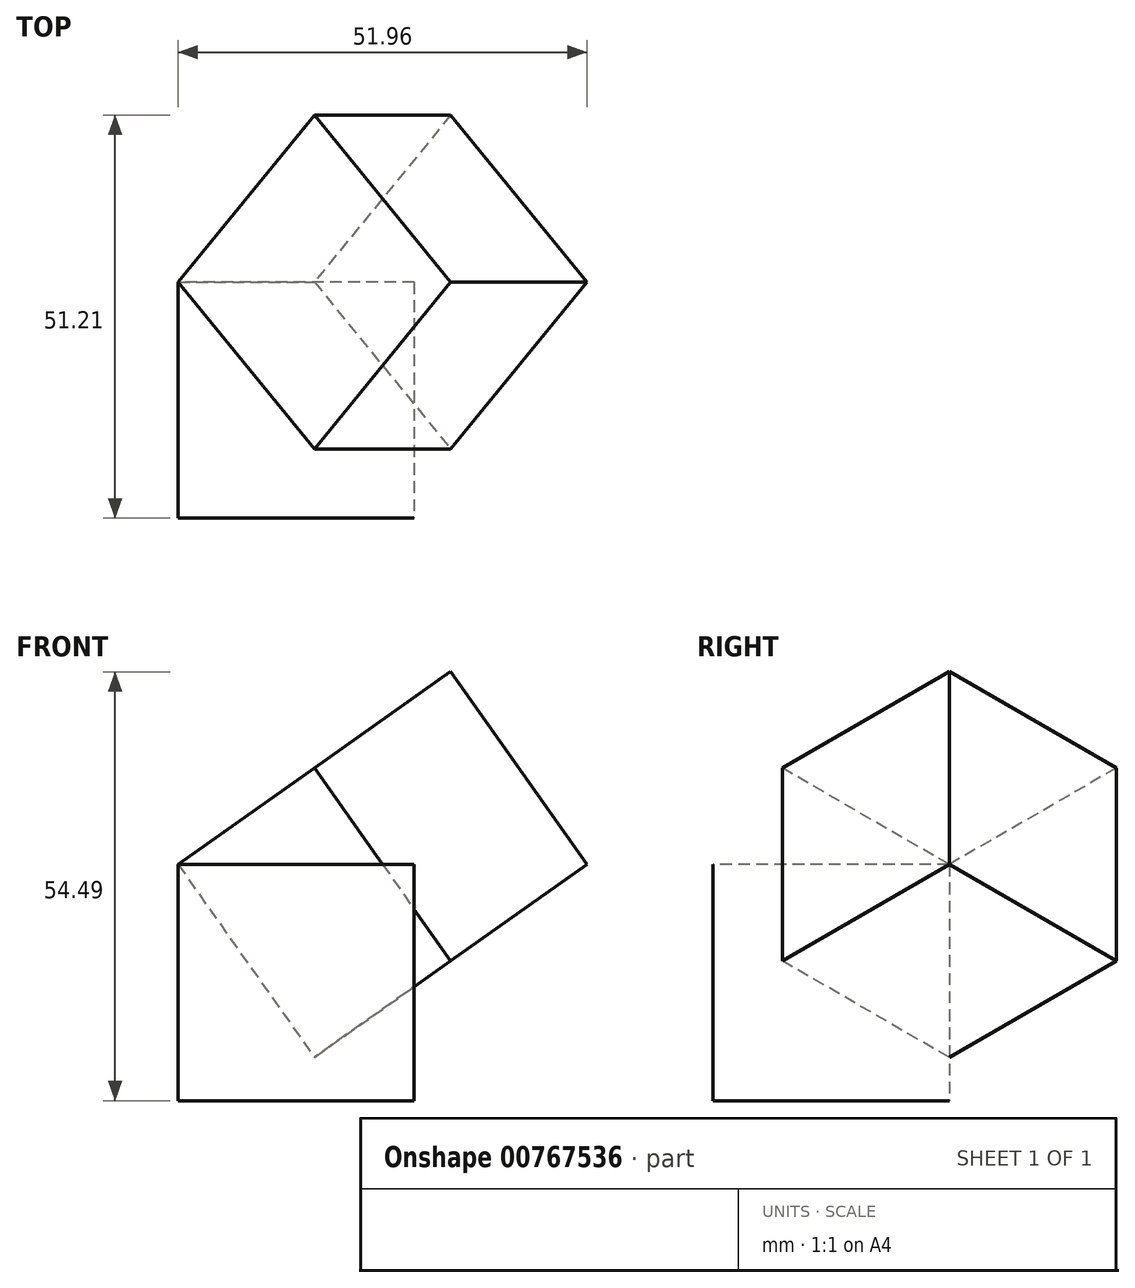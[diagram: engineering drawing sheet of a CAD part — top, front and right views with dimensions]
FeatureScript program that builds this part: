
annotation { "Feature Type Name" : "Feature", "Feature Type Description" : "" }
export const myFeature = defineFeature(function(context is Context, id is Id, definition is map)
    precondition{}
    {
        {
            var Q0;
            Q0=qCreatedBy(makeId("Top.planeOp"),FACE);
            var sketch = newSketch(context, id + "F0", { "sketchPlane" : qUnion([Q0])});
            skLineSegment(sketch, "E0.bottom", {"start": v(0, 0) * mm, "end": v(30, 0) * mm});
            skLineSegment(sketch, "E0.top", {"start": v(0, -30) * mm, "end": v(30, -30) * mm});
            skLineSegment(sketch, "E0.left", {"start": v(0, 0) * mm, "end": v(0, -30) * mm});
            skLineSegment(sketch, "E0.right", {"start": v(30, 0) * mm, "end": v(30, -30) * mm});
            skSolve(sketch);
        }
        {
            var Q0;
            Q0=makeQuery(id+"F0.imprint","IMPRINT",FACE,{"disambiguationData":[TD([[makeQuery(id+"F0.imprint","IMPRINT",EDGE,{"derivedFrom":sQuery(id+"F0.wireOp",EDGE,"E0.bottom")}),-1.0]])]});
            extrude(context, id + "F1", {"entities" : qUnion([Q0]), "depth" : 30 * mm, "offsetDistance" : 25.4 * mm});
        }
        {
            var Q0;
            Q0=qCreatedBy(makeId("Front.planeOp"),FACE);
            var sketch = newSketch(context, id + "F2", { "sketchPlane" : qUnion([Q0])});
            skLineSegment(sketch, "E1", {"start": v(0, 0) * mm, "end": v(0, 64.25) * mm, "construction": true});
            skLineSegment(sketch, "E2", {"start": v(0, 0) * mm, "end": v(68.76, 0) * mm, "construction": true});
            skSolve(sketch);
        }
        {
            var Q0;
            Q0=makeQuery(id+"F1.opExtrude","SWEPT_BODY",BODY,{"disambiguationData":[OSD([sQuery(id+"F0.wireOp",EDGE,"E0.bottom"),sQuery(id+"F0.wireOp",EDGE,"E0.top"),sQuery(id+"F0.wireOp",EDGE,"E0.left"),sQuery(id+"F0.wireOp",EDGE,"E0.right")])]});
            var Q1;
            Q1=sQuery(id+"F2.wireOp",EDGE,"E2");
            transform(context, id + "F3", {"entities" : qUnion([Q0]), "transformType" : TransformType.ROTATION, "transformAxis" : qUnion([Q1]), "angle" : 45 * degree, "oppositeDirection" : true, "makeCopy" : true});
        }
        {
            var Q0;
            Q0=qCreatedBy(makeId("Right.planeOp"),FACE);
            var sketch = newSketch(context, id + "F4", { "sketchPlane" : qUnion([Q0])});
            skLineSegment(sketch, "E3", {"start": v(0, 0) * mm, "end": v(-65.28, 0) * mm, "construction": true});
            skSolve(sketch);
        }
        {
            var Q0;
            Q0=makeQuery(id+"F3.opPattern","COPY",BODY,{"derivedFrom":makeQuery(id+"F1.opExtrude","SWEPT_BODY",BODY,{"disambiguationData":[OSD([sQuery(id+"F0.wireOp",EDGE,"E0.bottom"),sQuery(id+"F0.wireOp",EDGE,"E0.top"),sQuery(id+"F0.wireOp",EDGE,"E0.left"),sQuery(id+"F0.wireOp",EDGE,"E0.right")])]}),"instanceName":"1"});
            var Q1;
            Q1=sQuery(id+"F4.wireOp",EDGE,"E3");
            transform(context, id + "F5", {"entities" : qUnion([Q0]), "transformType" : TransformType.ROTATION, "transformAxis" : qUnion([Q1]), "angle" : 35.26 * degree, "makeCopy" : false});
        }
        {
            var Q0;
            Q0=makeQuery(id+"F3.opPattern","COPY",BODY,{"derivedFrom":makeQuery(id+"F1.opExtrude","SWEPT_BODY",BODY,{"disambiguationData":[OSD([sQuery(id+"F0.wireOp",EDGE,"E0.bottom"),sQuery(id+"F0.wireOp",EDGE,"E0.top"),sQuery(id+"F0.wireOp",EDGE,"E0.left"),sQuery(id+"F0.wireOp",EDGE,"E0.right")])]}),"instanceName":"1"});
            var Q1;
            Q1=makeQuery(id+"F1.opExtrude","SWEPT_BODY",BODY,{"disambiguationData":[OSD([sQuery(id+"F0.wireOp",EDGE,"E0.bottom"),sQuery(id+"F0.wireOp",EDGE,"E0.top"),sQuery(id+"F0.wireOp",EDGE,"E0.left"),sQuery(id+"F0.wireOp",EDGE,"E0.right")])]});
            var Q2;
            Q2=sQuery(id+"F4.wireOp",EDGE,"E3");
            transform(context, id + "F6", {"entities" : qUnion([Q0, Q1]), "transformType" : TransformType.ROTATION, "transformAxis" : qUnion([Q2]), "angle" : 90 * degree, "oppositeDirection" : true, "makeCopy" : false});
        }
    });
